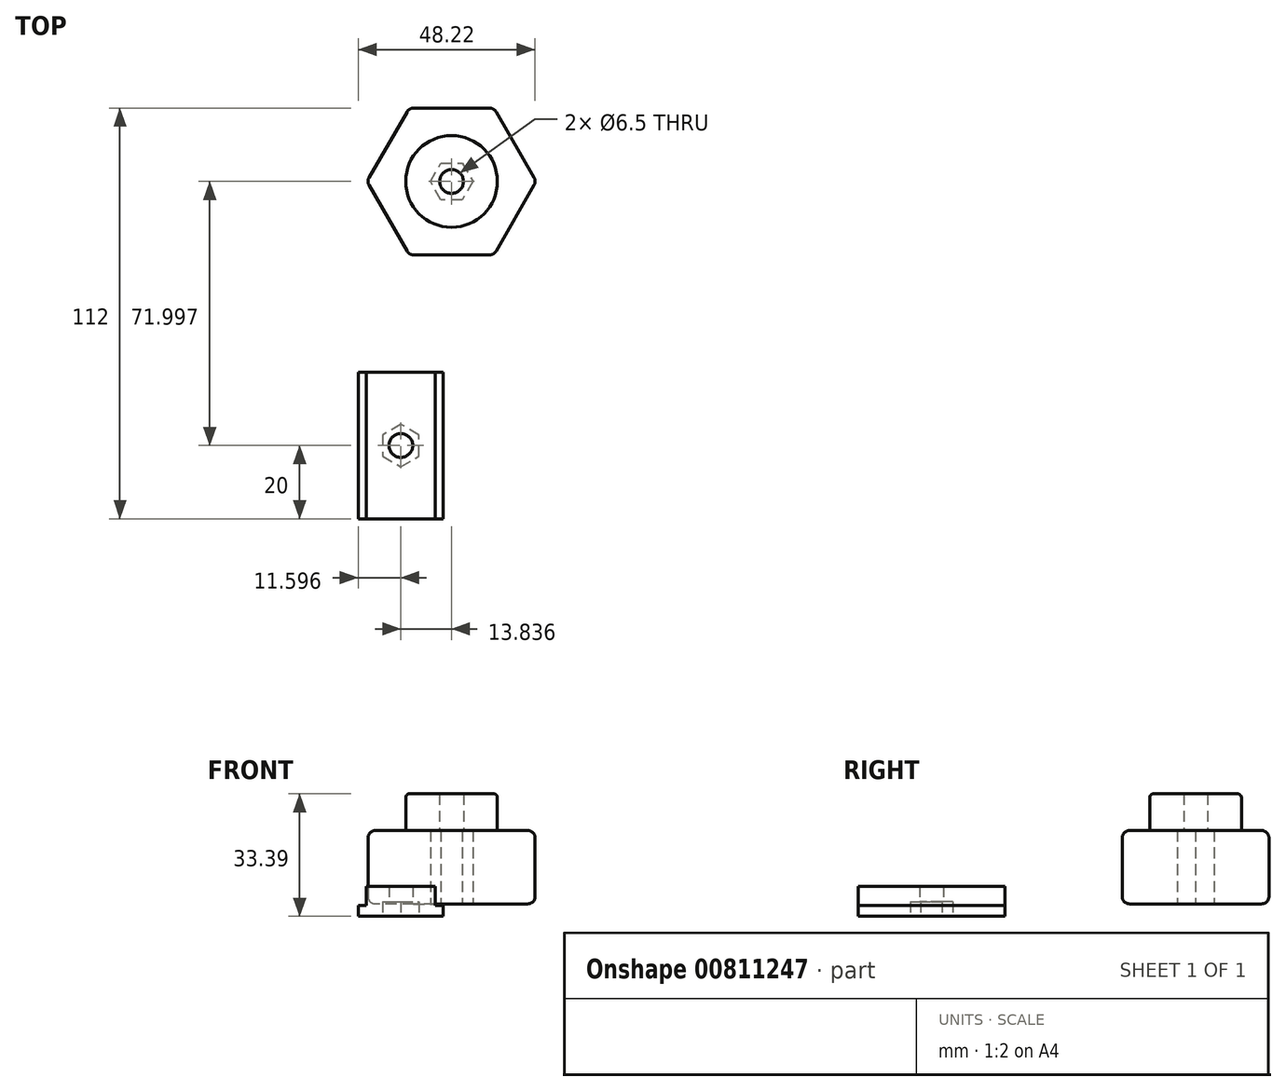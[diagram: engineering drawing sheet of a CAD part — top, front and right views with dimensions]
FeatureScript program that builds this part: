
annotation { "Feature Type Name" : "Feature", "Feature Type Description" : "" }
export const myFeature = defineFeature(function(context is Context, id is Id, definition is map)
    precondition{}
    {
        {
            var Q0;
            Q0=qCreatedBy(makeId("Front.planeOp"),FACE);
            var sketch = newSketch(context, id + "F0", { "sketchPlane" : qUnion([Q0])});
            skLineSegment(sketch, "E0.bottom", {"start": v(-9.98, -3.39) * mm, "end": v(13.22, -3.39) * mm});
            skLineSegment(sketch, "E0.top", {"start": v(-7.78, 4.81) * mm, "end": v(11.02, 4.81) * mm});
            skLineSegment(sketch, "E0.left", {"start": v(-9.98, -3.39) * mm, "end": v(-9.98, -0.39) * mm});
            skLineSegment(sketch, "E0.right", {"start": v(13.22, -3.39) * mm, "end": v(13.22, -0.39) * mm});
            skLineSegment(sketch, "E1.top", {"start": v(-9.98, -0.39) * mm, "end": v(-7.78, -0.39) * mm});
            skLineSegment(sketch, "E2.top", {"start": v(13.22, -0.39) * mm, "end": v(11.02, -0.39) * mm});
            skLineSegment(sketch, "E3", {"start": v(11.02, 4.81) * mm, "end": v(11.02, -0.39) * mm});
            skLineSegment(sketch, "E4", {"start": v(-7.78, 4.81) * mm, "end": v(-7.78, -0.39) * mm});
            skPoint(sketch, "E5.orphan", {"position": v(-2.6, -0.39) * mm});
            skPoint(sketch, "E6.orphan", {"position": v(7.5, -0.39) * mm});
            skSolve(sketch);
        }
        {
            var Q0;
            Q0=makeQuery(id+"F0.imprint","IMPRINT",FACE,{"disambiguationData":[TD([[makeQuery(id+"F0.imprint","IMPRINT",EDGE,{"derivedFrom":sQuery(id+"F0.wireOp",EDGE,"E0.bottom")}),1.0]])]});
            extrude(context, id + "F1", {"entities" : qUnion([Q0]), "depth" : 40 * mm, "offsetDistance" : 25 * mm});
        }
        {
            var Q0;
            Q0=makeQuery(id+"F1.opExtrude","SWEPT_FACE",FACE,{"disambiguationData":[OSD([sQuery(id+"F0.wireOp",EDGE,"E0.bottom")])]});
            var sketch = newSketch(context, id + "F2", { "sketchPlane" : qUnion([Q0])});
            skLineSegment(sketch, "E7", {"start": v(-9.98, 40) * mm, "end": v(13.22, 0) * mm});
            skLineSegment(sketch, "E8", {"start": v(13.22, 0) * mm, "end": v(13.22, 40) * mm});
            skLineSegment(sketch, "E9", {"start": v(13.22, 40) * mm, "end": v(-9.98, 0) * mm});
            skLineSegment(sketch, "E10", {"start": v(-9.98, 0) * mm, "end": v(1.62, 20) * mm});
            skCircle(sketch, "E11.cCircle", {"center": v(1.62, 20) * mm, "radius": 5 * mm, "construction": true});
            skLineSegment(sketch, "E11.0", {"start": v(6.62, 22.89) * mm, "end": v(6.62, 17.11) * mm});
            skLineSegment(sketch, "E11.1", {"start": v(6.62, 17.11) * mm, "end": v(1.62, 14.23) * mm});
            skLineSegment(sketch, "E11.2", {"start": v(1.62, 14.23) * mm, "end": v(-3.38, 17.11) * mm});
            skLineSegment(sketch, "E11.3", {"start": v(-3.38, 17.11) * mm, "end": v(-3.38, 22.89) * mm});
            skLineSegment(sketch, "E11.4", {"start": v(-3.38, 22.89) * mm, "end": v(1.62, 25.77) * mm});
            skLineSegment(sketch, "E11.5", {"start": v(1.62, 25.77) * mm, "end": v(6.62, 22.89) * mm});
            skPoint(sketch, "E11.0.midPoint", {"position": v(6.62, 20) * mm});
            skSolve(sketch);
        }
        {
            var Q0;
            {var subQ1=sQuery(id+"F2.wireOp",EDGE,"E11.0");Q0=makeQuery(id+"F2.imprint","IMPRINT",FACE,{"disambiguationData":[TD([[makeQuery(id+"F2.imprint","IMPRINT",EDGE,{"derivedFrom":subQ1}),-1.0]])]});}
            var Q1;
            {var subQ3=sQuery(id+"F2.wireOp",EDGE,"E11.4");var subQ5=sQuery(id+"F2.wireOp",EDGE,"E11.5");var subQ7=makeQuery(id+"F2.imprint","INTERSECT",VERTEX,{"derivedFrom":[subQ3,subQ5]});Q1=makeQuery(id+"F2.imprint","IMPRINT",FACE,{"disambiguationData":[TD([[makeQuery(id+"F2.imprint","IMPRINT",EDGE,{"disambiguationData":[TD([[subQ7,1.0]])],"derivedFrom":subQ3}),-1.0]])]});}
            var Q2;
            {var subQ0=sQuery(id+"F2.wireOp",EDGE,"E11.3");Q2=makeQuery(id+"F2.imprint","IMPRINT",FACE,{"disambiguationData":[TD([[makeQuery(id+"F2.imprint","IMPRINT",EDGE,{"derivedFrom":subQ0}),-1.0]])]});}
            var Q3;
            {var subQ3=sQuery(id+"F2.wireOp",EDGE,"E11.1");var subQ5=sQuery(id+"F2.wireOp",EDGE,"E11.2");var subQ6=makeQuery(id+"F2.imprint","INTERSECT",VERTEX,{"derivedFrom":[subQ3,subQ5]});Q3=makeQuery(id+"F2.imprint","IMPRINT",FACE,{"disambiguationData":[TD([[makeQuery(id+"F2.imprint","IMPRINT",EDGE,{"disambiguationData":[TD([[subQ6,1.0]])],"derivedFrom":subQ3}),-1.0]])]});}
            extrude(context, id + "F3", {"entities" : qUnion([Q0, Q1, Q2, Q3]), "operationType" : NewBodyOperationType.REMOVE, "oppositeDirection" : true, "depth" : 4 * mm, "offsetDistance" : 25 * mm});
        }
        {
            var Q0;
            Q0=sQuery(id+"F2.wireOp",VERTEX,"E10.end");
            var Q1;
            Q1=makeQuery(id+"F1.opExtrude","SWEPT_BODY",BODY,{"disambiguationData":[OSD([sQuery(id+"F0.wireOp",EDGE,"E0.bottom"),sQuery(id+"F0.wireOp",EDGE,"E0.top"),sQuery(id+"F0.wireOp",EDGE,"E0.left"),sQuery(id+"F0.wireOp",EDGE,"E0.right"),sQuery(id+"F0.wireOp",EDGE,"E1.top"),sQuery(id+"F0.wireOp",EDGE,"E2.top"),sQuery(id+"F0.wireOp",EDGE,"E3"),sQuery(id+"F0.wireOp",EDGE,"E4")])]});
            hole(context, id + "F4", {"style" : HoleStyle.SIMPLE, "endStyle" : HoleEndStyle.THROUGH, "holeDiameter" : 6.5 * mm, "majorDiameter" : 5 * mm, "isTappedThrough" : true, "tappedDepth" : 12 * mm, "tapClearance" : 3, "locations" : qUnion([Q0]), "scope" : qUnion([Q1])});
        }
        {
            var Q0;
            Q0=qCreatedBy(makeId("Top.planeOp"),FACE);
            var sketch = newSketch(context, id + "F5", { "sketchPlane" : qUnion([Q0])});
            skCircle(sketch, "E12.cCircle", {"center": v(15.45, 52) * mm, "radius": 20 * mm, "construction": true});
            skLineSegment(sketch, "E12.0", {"start": v(27, 32) * mm, "end": v(3.9, 32) * mm});
            skLineSegment(sketch, "E12.1", {"start": v(3.9, 32) * mm, "end": v(-7.64, 52) * mm});
            skLineSegment(sketch, "E12.2", {"start": v(-7.64, 52) * mm, "end": v(3.9, 72) * mm});
            skLineSegment(sketch, "E12.3", {"start": v(3.9, 72) * mm, "end": v(27, 72) * mm});
            skLineSegment(sketch, "E12.4", {"start": v(27, 72) * mm, "end": v(38.55, 52) * mm});
            skLineSegment(sketch, "E12.5", {"start": v(38.55, 52) * mm, "end": v(27, 32) * mm});
            skPoint(sketch, "E12.0.midPoint", {"position": v(15.45, 32) * mm});
            skCircle(sketch, "E13.cCircle", {"center": v(15.45, 52) * mm, "radius": 5 * mm, "construction": true});
            skLineSegment(sketch, "E13.0", {"start": v(18.34, 47) * mm, "end": v(12.57, 47) * mm});
            skLineSegment(sketch, "E13.1", {"start": v(12.57, 47) * mm, "end": v(9.68, 52) * mm});
            skLineSegment(sketch, "E13.2", {"start": v(9.68, 52) * mm, "end": v(12.57, 57) * mm});
            skLineSegment(sketch, "E13.3", {"start": v(12.57, 57) * mm, "end": v(18.34, 57) * mm});
            skLineSegment(sketch, "E13.4", {"start": v(18.34, 57) * mm, "end": v(21.23, 52) * mm});
            skLineSegment(sketch, "E13.5", {"start": v(21.23, 52) * mm, "end": v(18.34, 47) * mm});
            skPoint(sketch, "E13.0.midPoint", {"position": v(15.45, 47) * mm});
            skCircle(sketch, "E14", {"center": v(15.45, 52) * mm, "radius": 12.5 * mm});
            skSolve(sketch);
        }
        {
            var Q0;
            Q0=makeQuery(id+"F5.imprint","IMPRINT",FACE,{"disambiguationData":[TD([[makeQuery(id+"F5.imprint","IMPRINT",EDGE,{"derivedFrom":sQuery(id+"F5.wireOp",EDGE,"E12.0")}),-1.0]])]});
            extrude(context, id + "F6", {"entities" : qUnion([Q0]), "depth" : 20 * mm, "offsetDistance" : 25 * mm});
        }
        {
            var Q0;
            Q0=makeQuery(id+"F5.imprint","IMPRINT",FACE,{"disambiguationData":[TD([[makeQuery(id+"F5.imprint","IMPRINT",EDGE,{"derivedFrom":sQuery(id+"F5.wireOp",EDGE,"E13.0")}),1.0]])]});
            var Q1;
            Q1=makeQuery(id+"F5.imprint","IMPRINT",FACE,{"disambiguationData":[TD([[makeQuery(id+"F5.imprint","IMPRINT",EDGE,{"derivedFrom":sQuery(id+"F5.wireOp",EDGE,"E13.0")}),-1.0]])]});
            extrude(context, id + "F7", {"entities" : qUnion([Q0, Q1]), "operationType" : NewBodyOperationType.ADD, "depth" : 30 * mm, "offsetDistance" : 25 * mm});
        }
        {
            var Q0;
            Q0=makeQuery(id+"F5.imprint","IMPRINT",FACE,{"disambiguationData":[TD([[makeQuery(id+"F5.imprint","IMPRINT",EDGE,{"derivedFrom":sQuery(id+"F5.wireOp",EDGE,"E13.0")}),-1.0]])]});
            extrude(context, id + "F8", {"entities" : qUnion([Q0]), "operationType" : NewBodyOperationType.REMOVE, "depth" : 20 * mm, "offsetDistance" : 25 * mm});
        }
        {
            var Q0;
            Q0=sQuery(id+"F5.wireOp",VERTEX,"E12.cCircle.center");
            var Q1;
            Q1=makeQuery(id+"F6.opExtrude","SWEPT_BODY",BODY,{"disambiguationData":[OSD([sQuery(id+"F5.wireOp",EDGE,"E12.0"),sQuery(id+"F5.wireOp",EDGE,"E12.1"),sQuery(id+"F5.wireOp",EDGE,"E12.2"),sQuery(id+"F5.wireOp",EDGE,"E12.3"),sQuery(id+"F5.wireOp",EDGE,"E12.4"),sQuery(id+"F5.wireOp",EDGE,"E12.5"),sQuery(id+"F5.wireOp",EDGE,"E14")])]});
            hole(context, id + "F9", {"style" : HoleStyle.SIMPLE, "endStyle" : HoleEndStyle.THROUGH, "oppositeDirection" : true, "holeDiameter" : 6.5 * mm, "majorDiameter" : 5 * mm, "isTappedThrough" : true, "tappedDepth" : 12 * mm, "tapClearance" : 3, "locations" : qUnion([Q0]), "scope" : qUnion([Q1])});
        }
        {
            var Q0;
            Q0=makeQuery(id+"F6.opExtrude","SWEPT_EDGE",EDGE,{"disambiguationData":[OSD([sQuery(id+"F5.wireOp",EDGE,"E12.2"),sQuery(id+"F5.wireOp",EDGE,"E12.3")])]});
            var Q1;
            Q1=makeQuery(id+"F6.opExtrude","SWEPT_FACE",FACE,{"disambiguationData":[OSD([sQuery(id+"F5.wireOp",EDGE,"E12.3")])]});
            var Q2;
            Q2=makeQuery(id+"F6.opExtrude","SWEPT_FACE",FACE,{"disambiguationData":[OSD([sQuery(id+"F5.wireOp",EDGE,"E12.4")])]});
            var Q3;
            Q3=makeQuery(id+"F6.opExtrude","SWEPT_FACE",FACE,{"disambiguationData":[OSD([sQuery(id+"F5.wireOp",EDGE,"E12.2")])]});
            var Q4;
            Q4=makeQuery(id+"F6.opExtrude","SWEPT_FACE",FACE,{"disambiguationData":[OSD([sQuery(id+"F5.wireOp",EDGE,"E12.5")])]});
            var Q5;
            Q5=makeQuery(id+"F6.opExtrude","SWEPT_FACE",FACE,{"disambiguationData":[OSD([sQuery(id+"F5.wireOp",EDGE,"E12.0")])]});
            var Q6;
            Q6=makeQuery(id+"F6.opExtrude","SWEPT_FACE",FACE,{"disambiguationData":[OSD([sQuery(id+"F5.wireOp",EDGE,"E12.1")])]});
            fillet(context, id + "F10", {"entities" : qUnion([Q0, Q1, Q2, Q3, Q4, Q5, Q6]), "radius" : 2 * mm, "tangentPropagation" : true, "allowEdgeOverflow" : false});
        }
        {
            var Q0;
            Q0=makeQuery(id+"F7.opExtrude","CAP_EDGE",EDGE,{"disambiguationData":[OSD([sQuery(id+"F5.wireOp",EDGE,"E14")])],"isStart":false});
            var Q1;
            Q1=makeQuery(id+"F8.boolean.opBoolean","COPY",EDGE,{"derivedFrom":makeQuery(id+"F8.opExtrude","CAP_EDGE",EDGE,{"disambiguationData":[OSD([sQuery(id+"F5.wireOp",EDGE,"E13.0")])],"isStart":true})});
            var Q2;
            Q2=makeQuery(id+"F8.boolean.opBoolean","COPY",EDGE,{"derivedFrom":makeQuery(id+"F8.opExtrude","CAP_EDGE",EDGE,{"disambiguationData":[OSD([sQuery(id+"F5.wireOp",EDGE,"E13.1")])],"isStart":true})});
            var Q3;
            Q3=makeQuery(id+"F8.boolean.opBoolean","COPY",EDGE,{"derivedFrom":makeQuery(id+"F8.opExtrude","CAP_EDGE",EDGE,{"disambiguationData":[OSD([sQuery(id+"F5.wireOp",EDGE,"E13.2")])],"isStart":true})});
            var Q4;
            Q4=makeQuery(id+"F8.boolean.opBoolean","COPY",EDGE,{"derivedFrom":makeQuery(id+"F8.opExtrude","CAP_EDGE",EDGE,{"disambiguationData":[OSD([sQuery(id+"F5.wireOp",EDGE,"E13.3")])],"isStart":true})});
            var Q5;
            Q5=makeQuery(id+"F8.boolean.opBoolean","COPY",EDGE,{"derivedFrom":makeQuery(id+"F8.opExtrude","CAP_EDGE",EDGE,{"disambiguationData":[OSD([sQuery(id+"F5.wireOp",EDGE,"E13.4")])],"isStart":true})});
            var Q6;
            Q6=makeQuery(id+"F8.boolean.opBoolean","COPY",EDGE,{"derivedFrom":makeQuery(id+"F8.opExtrude","CAP_EDGE",EDGE,{"disambiguationData":[OSD([sQuery(id+"F5.wireOp",EDGE,"E13.5")])],"isStart":true})});
            fillet(context, id + "F11", {"entities" : qUnion([Q0, Q1, Q2, Q3, Q4, Q5, Q6]), "radius" : 1 * mm, "tangentPropagation" : true, "allowEdgeOverflow" : false});
        }
    });
